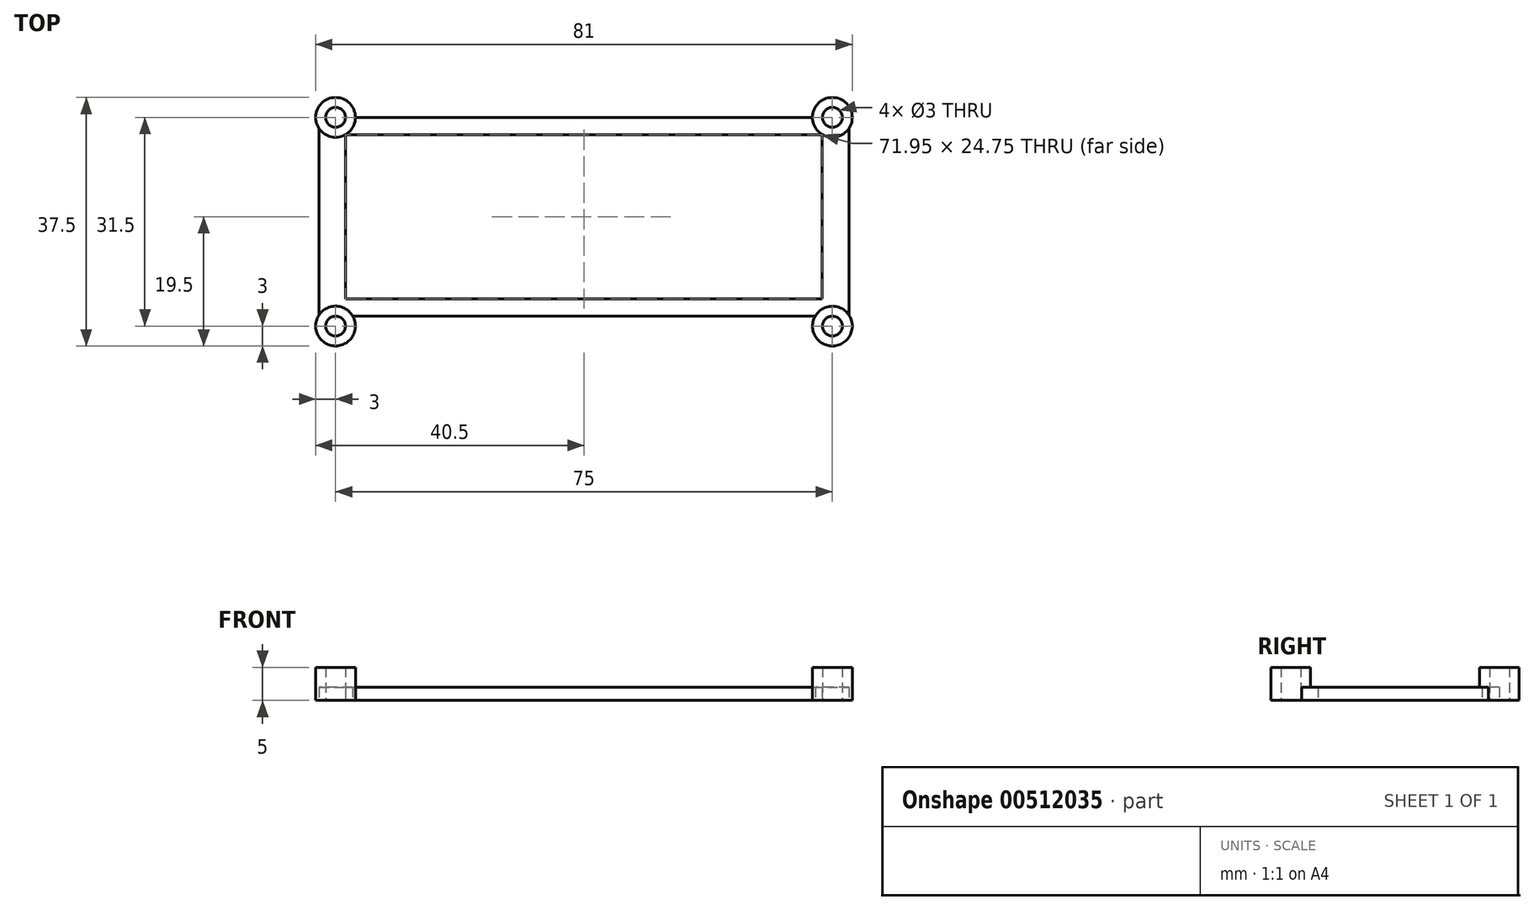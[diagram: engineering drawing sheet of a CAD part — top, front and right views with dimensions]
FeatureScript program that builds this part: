
annotation { "Feature Type Name" : "Feature", "Feature Type Description" : "" }
export const myFeature = defineFeature(function(context is Context, id is Id, definition is map)
    precondition{}
    {
        {
            var Q0;
            Q0=qCreatedBy(makeId("Top.planeOp"),FACE);
            var sketch = newSketch(context, id + "F0", { "sketchPlane" : qUnion([Q0])});
            skLineSegment(sketch, "E0.bottom", {"start": v(-40, 15) * mm, "end": v(40, 15) * mm});
            skLineSegment(sketch, "E0.top", {"start": v(-40, -15) * mm, "end": v(40, -15) * mm});
            skLineSegment(sketch, "E0.left", {"start": v(-40, 15) * mm, "end": v(-40, -15) * mm});
            skLineSegment(sketch, "E0.right", {"start": v(40, 15) * mm, "end": v(40, -15) * mm});
            skPoint(sketch, "E0.middle", {"position": v(0, 0) * mm});
            skLineSegment(sketch, "E1.bottom", {"start": v(-35.98, 12.37) * mm, "end": v(35.98, 12.37) * mm});
            skLineSegment(sketch, "E1.top", {"start": v(-35.98, -12.38) * mm, "end": v(35.98, -12.38) * mm});
            skLineSegment(sketch, "E1.left", {"start": v(-35.98, 12.37) * mm, "end": v(-35.98, -12.38) * mm});
            skLineSegment(sketch, "E1.right", {"start": v(35.98, 12.37) * mm, "end": v(35.98, -12.38) * mm});
            skCircle(sketch, "E2", {"center": v(-37.5, 15) * mm, "radius": 1.5 * mm});
            skCircle(sketch, "E3", {"center": v(37.5, 15) * mm, "radius": 1.5 * mm});
            skCircle(sketch, "E4", {"center": v(-37.5, -16.5) * mm, "radius": 1.5 * mm});
            skCircle(sketch, "E5", {"center": v(37.5, -16.5) * mm, "radius": 1.5 * mm});
            skCircle(sketch, "E6", {"center": v(-37.5, 15) * mm, "radius": 3 * mm});
            skCircle(sketch, "E7", {"center": v(37.5, 15) * mm, "radius": 3 * mm});
            skCircle(sketch, "E8", {"center": v(-37.5, -16.5) * mm, "radius": 3 * mm});
            skCircle(sketch, "E9", {"center": v(37.5, -16.5) * mm, "radius": 3 * mm});
            skLineSegment(sketch, "E10", {"start": v(-37.5, 15) * mm, "end": v(0, 0) * mm, "construction": true});
            skLineSegment(sketch, "E11", {"start": v(37.5, 15) * mm, "end": v(0, 0) * mm, "construction": true});
            skLineSegment(sketch, "E12", {"start": v(0, 0) * mm, "end": v(-37.5, -16.5) * mm, "construction": true});
            skLineSegment(sketch, "E13", {"start": v(0, 0) * mm, "end": v(37.5, -16.5) * mm, "construction": true});
            skSolve(sketch);
        }
        {
            var Q0;
            Q0=makeQuery(id+"F0.imprint","IMPRINT",FACE,{"disambiguationData":[TD([[makeQuery(id+"F0.imprint","IMPRINT",EDGE,{"derivedFrom":sQuery(id+"F0.wireOp",EDGE,"E1.bottom")}),1.0]])]});
            var Q1;
            {var subQ0=sQuery(id+"F0.wireOp",EDGE,"E6");var subQ1=sQuery(id+"F0.wireOp",EDGE,"E0.bottom");var subQ2=makeQuery(id+"F0.imprint","INTERSECT",VERTEX,{"derivedFrom":[subQ1,subQ0]});Q1=makeQuery(id+"F0.imprint","IMPRINT",FACE,{"disambiguationData":[TD([[makeQuery(id+"F0.imprint","IMPRINT",EDGE,{"disambiguationData":[TD([[subQ2,1.0]])],"derivedFrom":subQ1}),-1.0]])]});}
            var Q2;
            {var subQ0=sQuery(id+"F0.wireOp",EDGE,"E7");var subQ1=sQuery(id+"F0.wireOp",EDGE,"E0.bottom");var subQ2=makeQuery(id+"F0.imprint","INTERSECT",VERTEX,{"derivedFrom":[subQ1,subQ0]});Q2=makeQuery(id+"F0.imprint","IMPRINT",FACE,{"disambiguationData":[TD([[makeQuery(id+"F0.imprint","IMPRINT",EDGE,{"disambiguationData":[TD([[subQ2,-1.0]])],"derivedFrom":subQ1}),-1.0]])]});}
            var Q3;
            {var subQ0=sQuery(id+"F0.wireOp",EDGE,"E9");var subQ1=sQuery(id+"F0.wireOp",EDGE,"E0.top");var subQ2=makeQuery(id+"F0.imprint","INTERSECT",VERTEX,{"derivedFrom":[subQ1,subQ0]});Q3=makeQuery(id+"F0.imprint","IMPRINT",FACE,{"disambiguationData":[TD([[makeQuery(id+"F0.imprint","IMPRINT",EDGE,{"disambiguationData":[TD([[subQ2,-1.0]])],"derivedFrom":subQ1}),1.0]])]});}
            var Q4;
            {var subQ0=sQuery(id+"F0.wireOp",EDGE,"E0.left");var subQ1=sQuery(id+"F0.wireOp",EDGE,"E0.top");var subQ2=makeQuery(id+"F0.imprint","INTERSECT",VERTEX,{"derivedFrom":[subQ1,subQ0]});Q4=makeQuery(id+"F0.imprint","IMPRINT",FACE,{"disambiguationData":[TD([[makeQuery(id+"F0.imprint","IMPRINT",EDGE,{"disambiguationData":[TD([[subQ2,-1.0]])],"derivedFrom":subQ1}),1.0]])]});}
            extrude(context, id + "F1", {"entities" : qUnion([Q0, Q1, Q2, Q3, Q4]), "depth" : 2 * mm, "offsetDistance" : 25 * mm});
        }
        {
            var Q0;
            {var subQ0=sQuery(id+"F0.wireOp",EDGE,"E6");var subQ1=sQuery(id+"F0.wireOp",EDGE,"E0.bottom");var subQ2=makeQuery(id+"F0.imprint","INTERSECT",VERTEX,{"derivedFrom":[subQ1,subQ0]});Q0=makeQuery(id+"F0.imprint","IMPRINT",FACE,{"disambiguationData":[TD([[makeQuery(id+"F0.imprint","IMPRINT",EDGE,{"disambiguationData":[TD([[subQ2,1.0]])],"derivedFrom":subQ1}),-1.0]])]});}
            var Q1;
            {var subQ0=sQuery(id+"F0.wireOp",EDGE,"E6");var subQ1=sQuery(id+"F0.wireOp",EDGE,"E0.bottom");var subQ2=makeQuery(id+"F0.imprint","INTERSECT",VERTEX,{"derivedFrom":[subQ1,subQ0]});Q1=makeQuery(id+"F0.imprint","IMPRINT",FACE,{"disambiguationData":[TD([[makeQuery(id+"F0.imprint","IMPRINT",EDGE,{"disambiguationData":[TD([[subQ2,1.0]])],"derivedFrom":subQ1}),1.0]])]});}
            var Q2;
            {var subQ0=sQuery(id+"F0.wireOp",EDGE,"E4");Q2=makeQuery(id+"F0.imprint","IMPRINT",FACE,{"disambiguationData":[TD([[makeQuery(id+"F0.imprint","IMPRINT",EDGE,{"derivedFrom":subQ0}),-1.0]])]});}
            var Q3;
            {var subQ0=sQuery(id+"F0.wireOp",EDGE,"E0.left");var subQ1=sQuery(id+"F0.wireOp",EDGE,"E0.top");var subQ2=makeQuery(id+"F0.imprint","INTERSECT",VERTEX,{"derivedFrom":[subQ1,subQ0]});Q3=makeQuery(id+"F0.imprint","IMPRINT",FACE,{"disambiguationData":[TD([[makeQuery(id+"F0.imprint","IMPRINT",EDGE,{"disambiguationData":[TD([[subQ2,-1.0]])],"derivedFrom":subQ1}),1.0]])]});}
            var Q4;
            {var subQ0=sQuery(id+"F0.wireOp",EDGE,"E5");Q4=makeQuery(id+"F0.imprint","IMPRINT",FACE,{"disambiguationData":[TD([[makeQuery(id+"F0.imprint","IMPRINT",EDGE,{"derivedFrom":subQ0}),-1.0]])]});}
            var Q5;
            {var subQ0=sQuery(id+"F0.wireOp",EDGE,"E9");var subQ1=sQuery(id+"F0.wireOp",EDGE,"E0.top");var subQ2=makeQuery(id+"F0.imprint","INTERSECT",VERTEX,{"derivedFrom":[subQ1,subQ0]});Q5=makeQuery(id+"F0.imprint","IMPRINT",FACE,{"disambiguationData":[TD([[makeQuery(id+"F0.imprint","IMPRINT",EDGE,{"disambiguationData":[TD([[subQ2,-1.0]])],"derivedFrom":subQ1}),1.0]])]});}
            var Q6;
            {var subQ0=sQuery(id+"F0.wireOp",EDGE,"E7");var subQ1=sQuery(id+"F0.wireOp",EDGE,"E0.bottom");var subQ2=makeQuery(id+"F0.imprint","INTERSECT",VERTEX,{"derivedFrom":[subQ1,subQ0]});Q6=makeQuery(id+"F0.imprint","IMPRINT",FACE,{"disambiguationData":[TD([[makeQuery(id+"F0.imprint","IMPRINT",EDGE,{"disambiguationData":[TD([[subQ2,-1.0]])],"derivedFrom":subQ1}),1.0]])]});}
            var Q7;
            {var subQ0=sQuery(id+"F0.wireOp",EDGE,"E7");var subQ1=sQuery(id+"F0.wireOp",EDGE,"E0.bottom");var subQ2=makeQuery(id+"F0.imprint","INTERSECT",VERTEX,{"derivedFrom":[subQ1,subQ0]});Q7=makeQuery(id+"F0.imprint","IMPRINT",FACE,{"disambiguationData":[TD([[makeQuery(id+"F0.imprint","IMPRINT",EDGE,{"disambiguationData":[TD([[subQ2,-1.0]])],"derivedFrom":subQ1}),-1.0]])]});}
            extrude(context, id + "F2", {"entities" : qUnion([Q0, Q1, Q2, Q3, Q4, Q5, Q6, Q7]), "operationType" : NewBodyOperationType.ADD, "depth" : 5 * mm, "offsetDistance" : 25 * mm});
        }
    });
